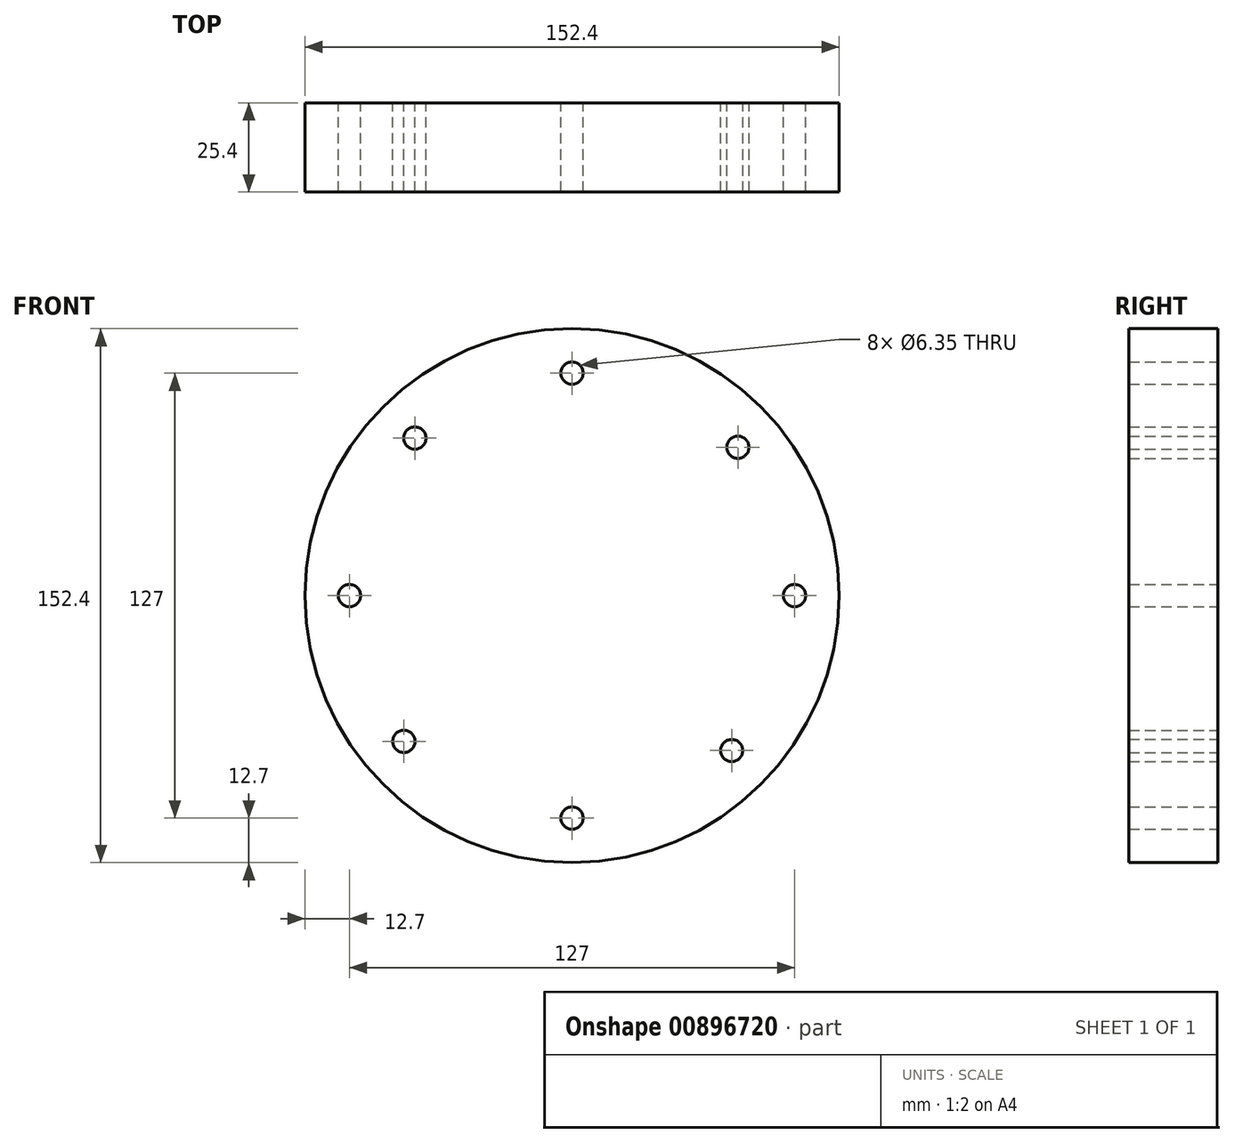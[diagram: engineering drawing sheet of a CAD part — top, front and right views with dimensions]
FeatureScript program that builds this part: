
annotation { "Feature Type Name" : "Feature", "Feature Type Description" : "" }
export const myFeature = defineFeature(function(context is Context, id is Id, definition is map)
    precondition{}
    {
        {
            var Q0;
            Q0=qCreatedBy(makeId("Front.planeOp"),FACE);
            var sketch = newSketch(context, id + "F0", { "sketchPlane" : qUnion([Q0])});
            skCircle(sketch, "E0", {"center": v(0, 0) * mm, "radius": 76.2 * mm});
            skCircle(sketch, "E1", {"center": v(0, 63.5) * mm, "radius": 3.18 * mm});
            skCircle(sketch, "E2", {"center": v(63.5, 0) * mm, "radius": 3.18 * mm});
            skCircle(sketch, "E3", {"center": v(0, -63.5) * mm, "radius": 3.18 * mm});
            skCircle(sketch, "E4", {"center": v(-63.5, 0) * mm, "radius": 3.18 * mm});
            skCircle(sketch, "E5", {"center": v(47.33, 42.33) * mm, "radius": 3.17 * mm});
            skCircle(sketch, "E6", {"center": v(45.56, -44.23) * mm, "radius": 3.18 * mm});
            skCircle(sketch, "E7", {"center": v(-47.97, -41.6) * mm, "radius": 3.18 * mm});
            skCircle(sketch, "E8", {"center": v(-44.84, 44.96) * mm, "radius": 3.18 * mm});
            skSolve(sketch);
        }
        {
            var Q0;
            Q0 = qSketchRegion(id + "F0", true);
            extrude(context, id + "F1", {"entities" : qUnion([Q0]), "depth" : 25.4 * mm, "offsetDistance" : 25.4 * mm});
        }
    });
